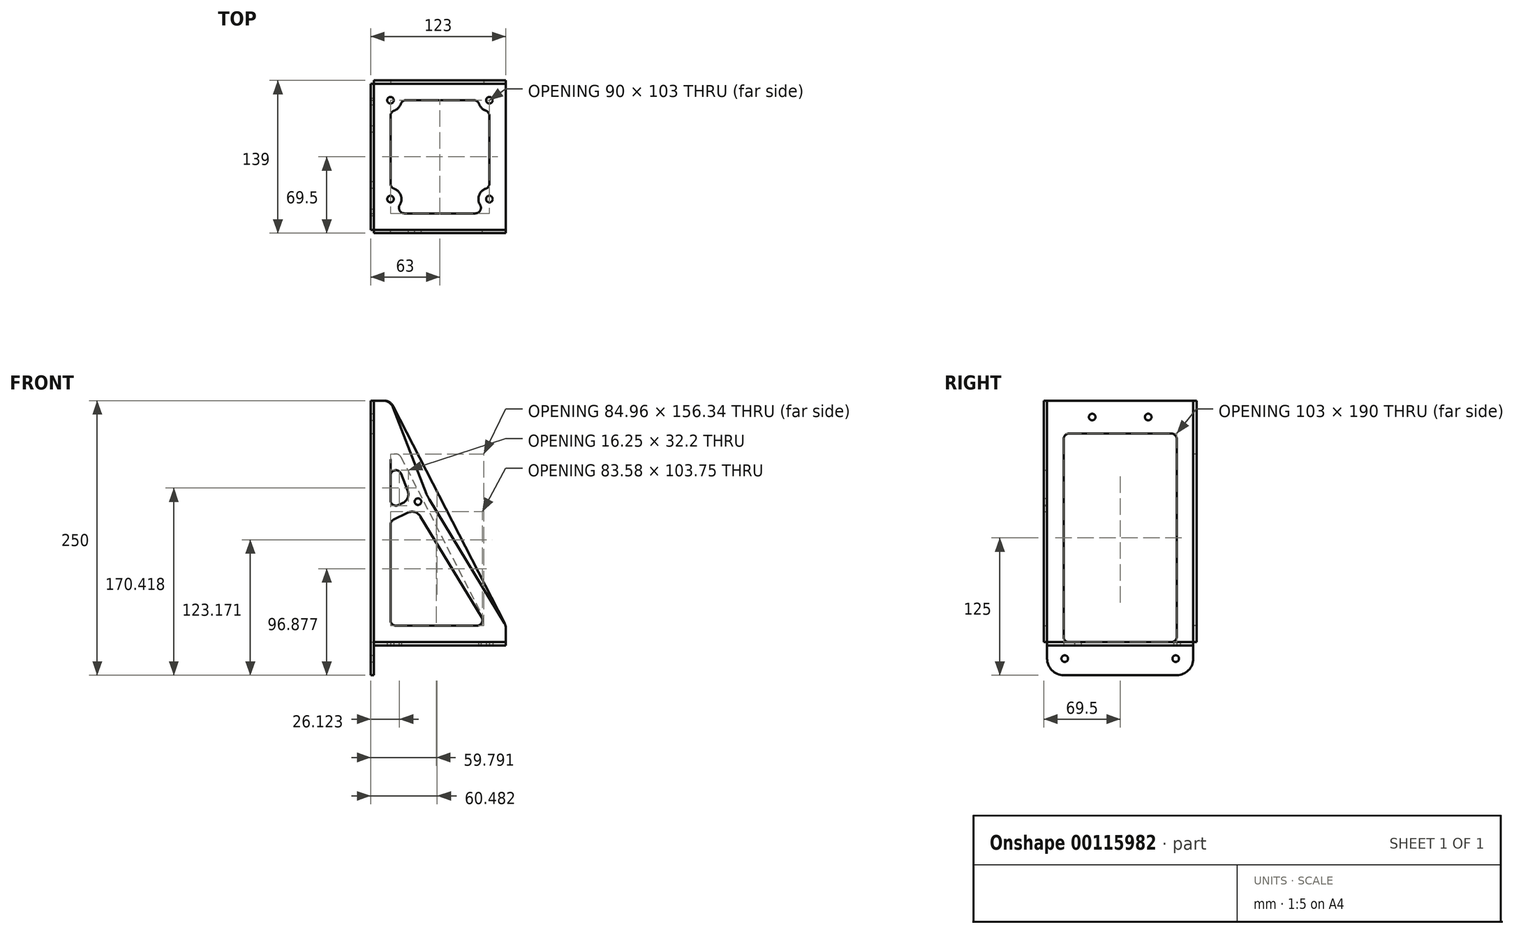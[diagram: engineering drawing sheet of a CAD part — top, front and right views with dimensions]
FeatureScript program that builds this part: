
annotation { "Feature Type Name" : "Feature", "Feature Type Description" : "" }
export const myFeature = defineFeature(function(context is Context, id is Id, definition is map)
    precondition{}
    {
        {
            var Q0;
            Q0=qCreatedBy(makeId("Top.planeOp"),FACE);
            var sketch = newSketch(context, id + "F0", { "sketchPlane" : qUnion([Q0])});
            skCircle(sketch, "E0", {"center": v(0, 0) * mm, "radius": 3 * mm});
            skCircle(sketch, "E1", {"center": v(0, 90) * mm, "radius": 3 * mm});
            skCircle(sketch, "E2", {"center": v(90, 0) * mm, "radius": 3 * mm});
            skCircle(sketch, "E3", {"center": v(90, 90) * mm, "radius": 3 * mm});
            skArc(sketch, "E4", {"start": v(3.33, 80.57) * mm, "mid": v(7.07, 82.93) * mm, "end": v(9.43, 86.67) * mm});
            skArc(sketch, "E5", {"start": v(80.57, 86.67) * mm, "mid": v(82.93, 82.93) * mm, "end": v(86.67, 80.57) * mm});
            skArc(sketch, "E6", {"start": v(86.67, 9.43) * mm, "mid": v(80.55, 3.28) * mm, "end": v(81.54, -5.33) * mm});
            skArc(sketch, "E7", {"start": v(8.46, -5.33) * mm, "mid": v(9.45, 3.28) * mm, "end": v(3.33, 9.43) * mm});
            skLineSegment(sketch, "E8.bottom", {"start": v(-15, 105) * mm, "end": v(105, 105) * mm});
            skLineSegment(sketch, "E8.top", {"start": v(-15, -28) * mm, "end": v(105, -28) * mm});
            skLineSegment(sketch, "E8.left", {"start": v(-15, 105) * mm, "end": v(-15, -28) * mm});
            skLineSegment(sketch, "E8.right", {"start": v(105, 105) * mm, "end": v(105, -28) * mm});
            skLineSegment(sketch, "E9", {"start": v(0, 75.86) * mm, "end": v(0, 14.14) * mm});
            skLineSegment(sketch, "E10", {"start": v(12.69, -13) * mm, "end": v(77.31, -13) * mm});
            skLineSegment(sketch, "E11", {"start": v(90, 14.14) * mm, "end": v(90, 75.86) * mm});
            skLineSegment(sketch, "E12", {"start": v(75.86, 90) * mm, "end": v(14.14, 90) * mm});
            skPoint(sketch, "E13.orphan", {"position": v(0, 80) * mm});
            skPoint(sketch, "E14.orphan", {"position": v(80, 90) * mm});
            skPoint(sketch, "E15.orphan", {"position": v(90, 10) * mm});
            skPoint(sketch, "E16.orphan", {"position": v(0, -10) * mm});
            skArc(sketch, "E17.filletArc", {"start": v(3.33, 80.57) * mm, "mid": v(0.92, 78.74) * mm, "end": v(0, 75.86) * mm});
            skPoint(sketch, "E18.visualSharp", {"position": v(10, 90) * mm});
            skArc(sketch, "E18.filletArc", {"start": v(14.14, 90) * mm, "mid": v(11.26, 89.08) * mm, "end": v(9.43, 86.67) * mm});
            skArc(sketch, "E19.filletArc", {"start": v(80.57, 86.67) * mm, "mid": v(78.74, 89.08) * mm, "end": v(75.86, 90) * mm});
            skPoint(sketch, "E20.visualSharp", {"position": v(90, 80) * mm});
            skArc(sketch, "E20.filletArc", {"start": v(90, 75.86) * mm, "mid": v(89.08, 78.74) * mm, "end": v(86.67, 80.57) * mm});
            skArc(sketch, "E21.filletArc", {"start": v(86.67, 9.43) * mm, "mid": v(89.08, 11.26) * mm, "end": v(90, 14.14) * mm});
            skPoint(sketch, "E22.visualSharp", {"position": v(0, 10) * mm});
            skArc(sketch, "E22.filletArc", {"start": v(0, 14.14) * mm, "mid": v(0.92, 11.26) * mm, "end": v(3.33, 9.43) * mm});
            skArc(sketch, "E23", {"start": v(8.46, -5.33) * mm, "mid": v(8.31, -10.42) * mm, "end": v(12.69, -13) * mm});
            skArc(sketch, "E24", {"start": v(77.31, -13) * mm, "mid": v(81.69, -10.42) * mm, "end": v(81.54, -5.33) * mm});
            skPoint(sketch, "E25.start.orphan", {"position": v(90, -13) * mm});
            skLineSegment(sketch, "E26", {"start": v(20, 2) * mm, "end": v(70, 2) * mm});
            skLineSegment(sketch, "E27", {"start": v(15, 7) * mm, "end": v(15, 70) * mm});
            skLineSegment(sketch, "E28", {"start": v(20, 75) * mm, "end": v(70, 75) * mm});
            skLineSegment(sketch, "E29", {"start": v(75, 70) * mm, "end": v(75, 7) * mm});
            skPoint(sketch, "E30.visualSharp", {"position": v(75, 75) * mm});
            skArc(sketch, "E30.filletArc", {"start": v(75, 70) * mm, "mid": v(73.54, 73.54) * mm, "end": v(70, 75) * mm});
            skPoint(sketch, "E31.visualSharp", {"position": v(15, 75) * mm});
            skArc(sketch, "E31.filletArc", {"start": v(20, 75) * mm, "mid": v(16.46, 73.54) * mm, "end": v(15, 70) * mm});
            skPoint(sketch, "E32.visualSharp", {"position": v(15, 2) * mm});
            skArc(sketch, "E32.filletArc", {"start": v(15, 7) * mm, "mid": v(16.46, 3.46) * mm, "end": v(20, 2) * mm});
            skPoint(sketch, "E33.visualSharp", {"position": v(75, 2) * mm});
            skArc(sketch, "E33.filletArc", {"start": v(70, 2) * mm, "mid": v(73.54, 3.46) * mm, "end": v(75, 7) * mm});
            skSolve(sketch);
        }
        {
            var Q0;
            Q0 = qSketchRegion(id + "F0", true);
            extrude(context, id + "F1", {"entities" : qUnion([Q0]), "depth" : 3 * mm});
        }
        {
            var Q0;
            Q0=makeQuery(id+"F1.opExtrude","SWEPT_FACE",FACE,{"disambiguationData":[OSD([sQuery(id+"F0.wireOp",EDGE,"E8.left")])]});
            var sketch = newSketch(context, id + "F2", { "sketchPlane" : qUnion([Q0])});
            skLineSegment(sketch, "E34.0", {"start": v(-85, 3) * mm, "end": v(8, 3) * mm, "construction": true});
            skCircle(sketch, "E35", {"center": v(-89, -12) * mm, "radius": 3 * mm});
            skCircle(sketch, "E36", {"center": v(12, -12) * mm, "radius": 3 * mm});
            skCircle(sketch, "E37", {"center": v(-13, 208) * mm, "radius": 3 * mm});
            skLineSegment(sketch, "E38.top", {"start": v(-105, 223) * mm, "end": v(28, 223) * mm});
            skLineSegment(sketch, "E38.left", {"start": v(-105, 3) * mm, "end": v(-105, 223) * mm});
            skLineSegment(sketch, "E38.right", {"start": v(28, 3) * mm, "end": v(28, 223) * mm});
            skLineSegment(sketch, "E39", {"start": v(-85, 3) * mm, "end": v(8, 3) * mm});
            skLineSegment(sketch, "E40", {"start": v(13, 8) * mm, "end": v(13, 188) * mm});
            skLineSegment(sketch, "E41", {"start": v(-90, 188) * mm, "end": v(-90, 8) * mm});
            skPoint(sketch, "E42.newPointB", {"position": v(-105, 3) * mm});
            skArc(sketch, "E42.filletArc", {"start": v(-90, 8) * mm, "mid": v(-88.54, 4.46) * mm, "end": v(-85, 3) * mm});
            skPoint(sketch, "E43.newPointB", {"position": v(28, 3) * mm});
            skArc(sketch, "E43.filletArc", {"start": v(8, 3) * mm, "mid": v(11.54, 4.46) * mm, "end": v(13, 8) * mm});
            skPoint(sketch, "E44.orphan", {"position": v(-90, 3) * mm});
            skLineSegment(sketch, "E45", {"start": v(-105, 3) * mm, "end": v(-105, -12) * mm});
            skLineSegment(sketch, "E46", {"start": v(-90, -27) * mm, "end": v(13, -27) * mm});
            skLineSegment(sketch, "E47", {"start": v(28, -12) * mm, "end": v(28, 3) * mm});
            skPoint(sketch, "E48.visualSharp", {"position": v(-105, -27) * mm});
            skArc(sketch, "E48.filletArc", {"start": v(-105, -12) * mm, "mid": v(-100.6, -22.6) * mm, "end": v(-90, -27) * mm});
            skPoint(sketch, "E49.visualSharp", {"position": v(28, -27) * mm});
            skArc(sketch, "E49.filletArc", {"start": v(13, -27) * mm, "mid": v(23.6, -22.6) * mm, "end": v(28, -12) * mm});
            skCircle(sketch, "E50", {"center": v(-64, 208) * mm, "radius": 3 * mm});
            skLineSegment(sketch, "E51", {"start": v(-85, 193) * mm, "end": v(8, 193) * mm});
            skPoint(sketch, "E52.visualSharp", {"position": v(-90, 193) * mm});
            skArc(sketch, "E52.filletArc", {"start": v(-85, 193) * mm, "mid": v(-88.54, 191.54) * mm, "end": v(-90, 188) * mm});
            skPoint(sketch, "E53.visualSharp", {"position": v(13, 193) * mm});
            skArc(sketch, "E53.filletArc", {"start": v(13, 188) * mm, "mid": v(11.54, 191.54) * mm, "end": v(8, 193) * mm});
            skSolve(sketch);
        }
        {
            var Q0;
            Q0 = qSketchRegion(id + "F2", true);
            extrude(context, id + "F3", {"entities" : qUnion([Q0]), "depth" : 3 * mm});
        }
        {
            var Q0;
            Q0=makeQuery(id+"F1.opExtrude","SWEPT_FACE",FACE,{"disambiguationData":[OSD([sQuery(id+"F0.wireOp",EDGE,"E8.bottom")])]});
            var sketch = newSketch(context, id + "F4", { "sketchPlane" : qUnion([Q0])});
            skLineSegment(sketch, "E54.0", {"start": v(15, 3) * mm, "end": v(-105, 3) * mm});
            skLineSegment(sketch, "E55.0", {"start": v(15, 223) * mm, "end": v(15, 223) * mm});
            skLineSegment(sketch, "E56", {"start": v(15, 223) * mm, "end": v(6.11, 223) * mm});
            skLineSegment(sketch, "E57", {"start": v(-2.79, 217.56) * mm, "end": v(-103.9, 20.15) * mm});
            skLineSegment(sketch, "E58", {"start": v(-105, 15.59) * mm, "end": v(-105, 3) * mm});
            skPoint(sketch, "E59.visualSharp", {"position": v(0, 223) * mm});
            skArc(sketch, "E59.filletArc", {"start": v(6.11, 223) * mm, "mid": v(0.9, 221.53) * mm, "end": v(-2.79, 217.56) * mm});
            skPoint(sketch, "E60.visualSharp", {"position": v(-105, 18) * mm});
            skArc(sketch, "E60.filletArc", {"start": v(-103.9, 20.15) * mm, "mid": v(-104.72, 17.93) * mm, "end": v(-105, 15.59) * mm});
            skLineSegment(sketch, "E61", {"start": v(-79.97, 18) * mm, "end": v(-5, 18) * mm});
            skLineSegment(sketch, "E62", {"start": v(0, 23) * mm, "end": v(0, 169.37) * mm});
            skLineSegment(sketch, "E63", {"start": v(-9.45, 171.65) * mm, "end": v(-84.42, 25.28) * mm});
            skPoint(sketch, "E64.visualSharp", {"position": v(0, 190.1) * mm});
            skArc(sketch, "E64.filletArc", {"start": v(0, 169.37) * mm, "mid": v(-3.83, 174.23) * mm, "end": v(-9.45, 171.65) * mm});
            skPoint(sketch, "E65.visualSharp", {"position": v(-88.15, 18) * mm});
            skArc(sketch, "E65.filletArc", {"start": v(-84.42, 25.28) * mm, "mid": v(-84.23, 20.4) * mm, "end": v(-79.97, 18) * mm});
            skPoint(sketch, "E66.visualSharp", {"position": v(0, 18) * mm});
            skArc(sketch, "E66.filletArc", {"start": v(-5, 18) * mm, "mid": v(-1.46, 19.46) * mm, "end": v(0, 23) * mm});
            skLineSegment(sketch, "E67.0", {"start": v(15, 223) * mm, "end": v(15, -12) * mm});
            skSolve(sketch);
        }
        {
            var Q0;
            Q0 = qSketchRegion(id + "F4", true);
            extrude(context, id + "F5", {"entities" : qUnion([Q0]), "depth" : 3 * mm});
        }
        {
            var Q0;
            Q0=makeQuery(id+"F1.opExtrude","SWEPT_FACE",FACE,{"disambiguationData":[OSD([sQuery(id+"F0.wireOp",EDGE,"E8.top")])]});
            var sketch = newSketch(context, id + "F6", { "sketchPlane" : qUnion([Q0])});
            skLineSegment(sketch, "E68.0", {"start": v(-15, 3) * mm, "end": v(105, 3) * mm});
            skLineSegment(sketch, "E69.0", {"start": v(-15, 223) * mm, "end": v(-15, 223) * mm});
            skCircle(sketch, "E70", {"center": v(25, 131) * mm, "radius": 3 * mm});
            skCircle(sketch, "E71", {"center": v(25, 131) * mm, "radius": 10 * mm, "construction": true});
            skArc(sketch, "E72", {"start": v(32.92, 137.83) * mm, "mid": v(33.98, 135.4) * mm, "end": v(35.24, 133.1) * mm});
            skLineSegment(sketch, "E73", {"start": v(-15, 223) * mm, "end": v(-6.86, 223) * mm});
            skLineSegment(sketch, "E74", {"start": v(2.47, 216.6) * mm, "end": v(32.92, 137.83) * mm});
            skLineSegment(sketch, "E75", {"start": v(105, 3) * mm, "end": v(105, 15.2) * mm});
            skLineSegment(sketch, "E76", {"start": v(103.55, 20.39) * mm, "end": v(35.24, 133.1) * mm});
            skLineSegment(sketch, "E77", {"start": v(60.9, 148.64) * mm, "end": v(-15, 111.34) * mm, "construction": true});
            skLineSegment(sketch, "E78.trimOffspring", {"start": v(33.87, 135.36) * mm, "end": v(33.87, 135.36) * mm});
            skPoint(sketch, "E79.visualSharp", {"position": v(105, 18) * mm});
            skArc(sketch, "E79.filletArc", {"start": v(105, 15.2) * mm, "mid": v(104.63, 17.9) * mm, "end": v(103.55, 20.39) * mm});
            skPoint(sketch, "E80.visualSharp", {"position": v(0, 223) * mm});
            skArc(sketch, "E80.filletArc", {"start": v(2.47, 216.6) * mm, "mid": v(-1.2, 221.25) * mm, "end": v(-6.86, 223) * mm});
            skLineSegment(sketch, "E81", {"start": v(7.2, 127.83) * mm, "end": v(11.35, 129.86) * mm});
            skLineSegment(sketch, "E82", {"start": v(2.8, 114.52) * mm, "end": v(15.76, 120.89) * mm});
            skLineSegment(sketch, "E83", {"start": v(0, 154.58) * mm, "end": v(0, 132.31) * mm});
            skLineSegment(sketch, "E84", {"start": v(5, 18) * mm, "end": v(78.58, 18) * mm});
            skLineSegment(sketch, "E85", {"start": v(82.86, 25.6) * mm, "end": v(27.11, 117.57) * mm});
            skLineSegment(sketch, "E86", {"start": v(9.66, 156.38) * mm, "end": v(15.66, 140.88) * mm});
            skLineSegment(sketch, "E87.trimOffspring", {"start": v(20.36, 128.72) * mm, "end": v(20.36, 128.71) * mm});
            skLineSegment(sketch, "E88.trimOffspring", {"start": v(20.36, 128.71) * mm, "end": v(20.36, 128.72) * mm});
            skPoint(sketch, "E89.visualSharp", {"position": v(22.96, 124.42) * mm});
            skArc(sketch, "E89.filletArc", {"start": v(27.11, 117.57) * mm, "mid": v(22.08, 121.43) * mm, "end": v(15.76, 120.89) * mm});
            skLineSegment(sketch, "E90.trimOffspring", {"start": v(104.6, 18) * mm, "end": v(105, 18) * mm});
            skPoint(sketch, "E91.visualSharp", {"position": v(87.46, 18) * mm});
            skArc(sketch, "E91.filletArc", {"start": v(78.58, 18) * mm, "mid": v(82.94, 20.55) * mm, "end": v(82.86, 25.6) * mm});
            skPoint(sketch, "E92.visualSharp", {"position": v(0, 18) * mm});
            skArc(sketch, "E92.filletArc", {"start": v(0, 23) * mm, "mid": v(1.46, 19.46) * mm, "end": v(5, 18) * mm});
            skLineSegment(sketch, "E93.trimOffspring", {"start": v(0, 110.03) * mm, "end": v(0, 23) * mm});
            skPoint(sketch, "E94.visualSharp", {"position": v(0, 113.14) * mm});
            skArc(sketch, "E94.filletArc", {"start": v(2.8, 114.52) * mm, "mid": v(0.76, 112.67) * mm, "end": v(0, 110.03) * mm});
            skPoint(sketch, "E95.visualSharp", {"position": v(0, 181.39) * mm});
            skArc(sketch, "E95.filletArc", {"start": v(9.66, 156.38) * mm, "mid": v(4.08, 159.5) * mm, "end": v(0, 154.58) * mm});
            skPoint(sketch, "E96.visualSharp", {"position": v(0, 124.29) * mm});
            skArc(sketch, "E96.filletArc", {"start": v(0, 132.31) * mm, "mid": v(2.36, 128.07) * mm, "end": v(7.2, 127.83) * mm});
            skPoint(sketch, "E97.visualSharp", {"position": v(18.55, 133.4) * mm});
            skArc(sketch, "E97.filletArc", {"start": v(11.35, 129.86) * mm, "mid": v(15.64, 134.53) * mm, "end": v(15.66, 140.88) * mm});
            skCircle(sketch, "E98", {"center": v(62, 131) * mm, "radius": 21.8 * mm, "construction": true});
            skLineSegment(sketch, "E99.0", {"start": v(-15, -12) * mm, "end": v(-15, 223) * mm});
            skSolve(sketch);
        }
        {
            var Q0;
            Q0 = qSketchRegion(id + "F6", true);
            extrude(context, id + "F7", {"entities" : qUnion([Q0]), "depth" : 3 * mm});
        }
    });
